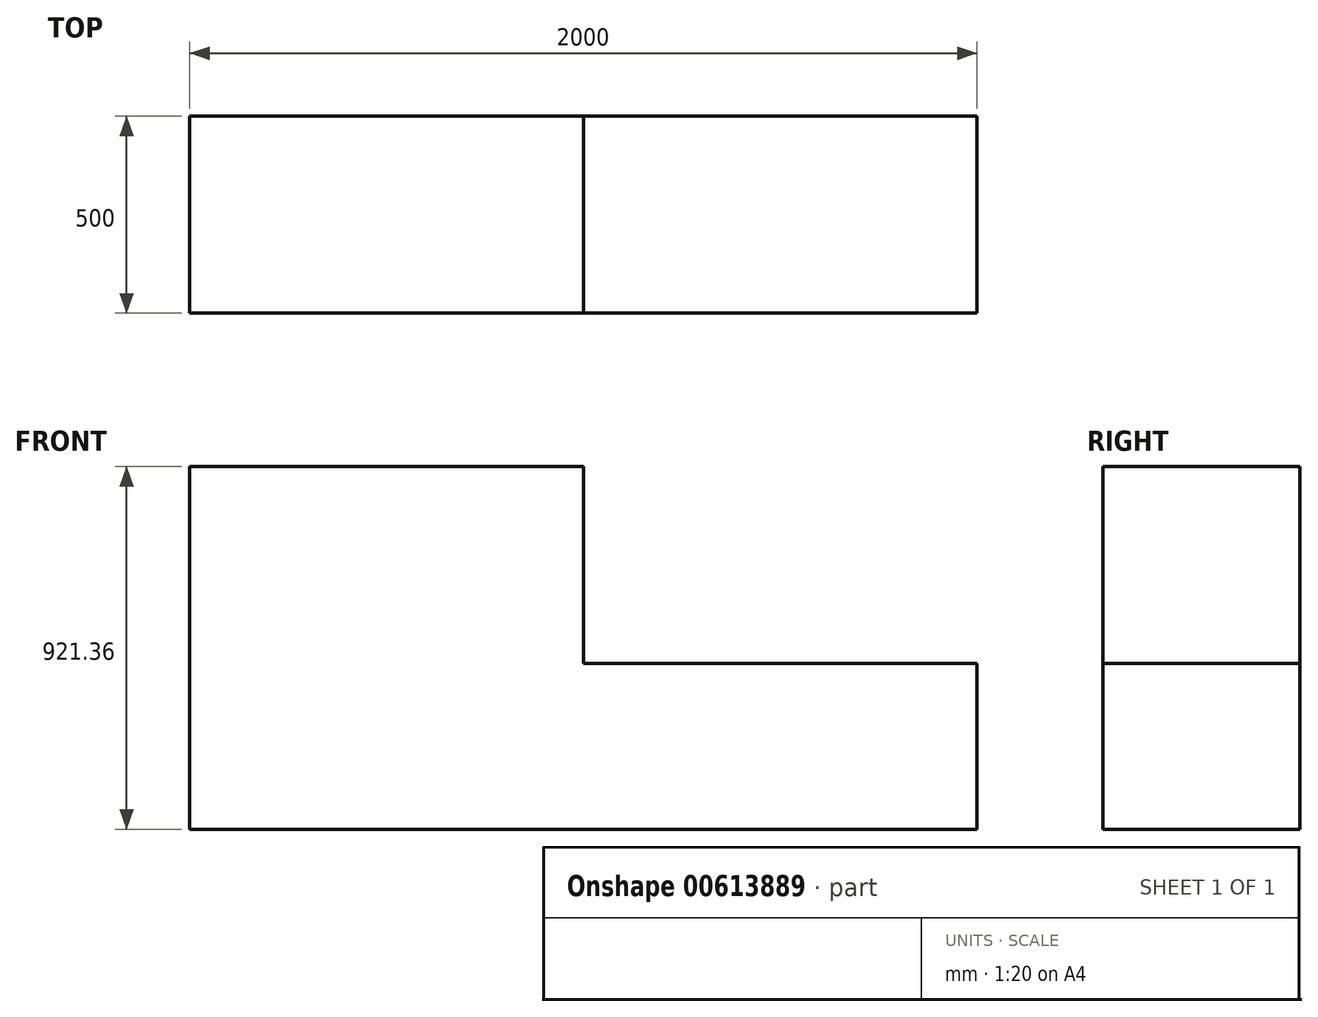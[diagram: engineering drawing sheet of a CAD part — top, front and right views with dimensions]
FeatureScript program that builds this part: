
annotation { "Feature Type Name" : "Feature", "Feature Type Description" : "" }
export const myFeature = defineFeature(function(context is Context, id is Id, definition is map)
    precondition{}
    {
        {
            var Q0;
            Q0=qCreatedBy(makeId("Front.planeOp"),FACE);
            var sketch = newSketch(context, id + "F0", { "sketchPlane" : qUnion([Q0])});
            skLineSegment(sketch, "E0", {"start": v(0, 0) * mm, "end": v(0, 921.36) * mm});
            skLineSegment(sketch, "E1", {"start": v(0, 921.36) * mm, "end": v(1000, 921.36) * mm});
            skLineSegment(sketch, "E2", {"start": v(1000, 921.36) * mm, "end": v(1000, 421.36) * mm});
            skLineSegment(sketch, "E3", {"start": v(1000, 421.36) * mm, "end": v(2000, 421.36) * mm});
            skLineSegment(sketch, "E4", {"start": v(2000, 421.36) * mm, "end": v(2000, 0) * mm});
            skLineSegment(sketch, "E5", {"start": v(2000, 0) * mm, "end": v(0, 0) * mm});
            skSolve(sketch);
        }
        {
            var Q0;
            Q0 = qSketchRegion(id + "F0", true);
            extrude(context, id + "F1", {"entities" : qUnion([Q0]), "depth" : 500 * mm, "offsetDistance" : 25 * mm});
        }
    });
